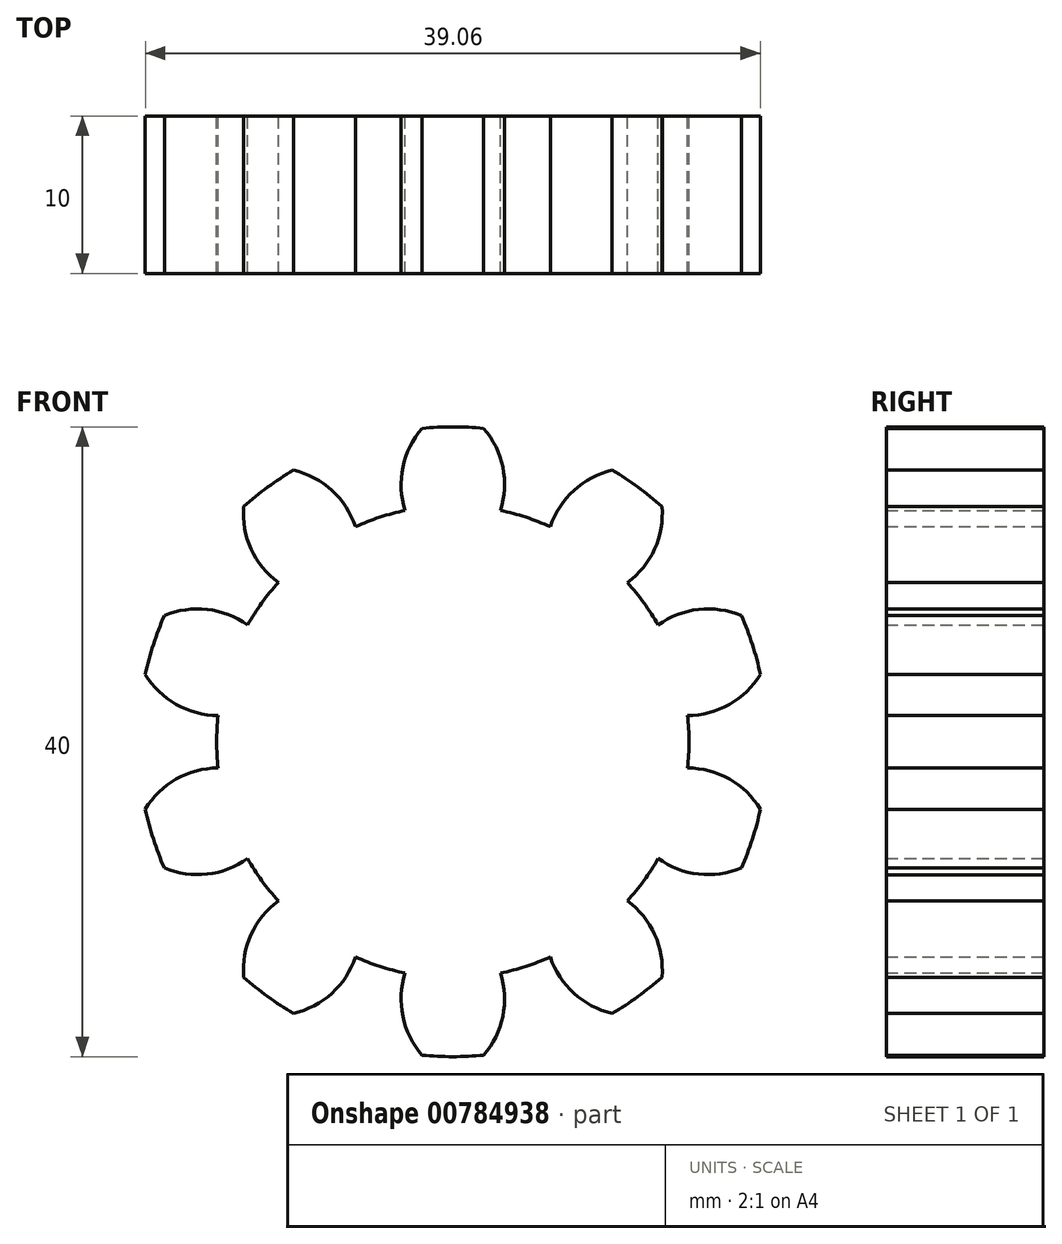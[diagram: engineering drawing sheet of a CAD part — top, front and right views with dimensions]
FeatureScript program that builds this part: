
annotation { "Feature Type Name" : "Feature", "Feature Type Description" : "" }
export const myFeature = defineFeature(function(context is Context, id is Id, definition is map)
    precondition{}
    {
        {
            var Q0;
            Q0=qCreatedBy(makeId("Front.planeOp"),FACE);
            var sketch = newSketch(context, id + "F0", { "sketchPlane" : qUnion([Q0])});
            skArc(sketch, "E0", {"start": v(1.96, 19.9) * mm, "mid": v(0, 20) * mm, "end": v(-1.96, 19.9) * mm});
            skArc(sketch, "E1.0", {"start": v(6.19, 13.66) * mm, "mid": v(4.64, 14.27) * mm, "end": v(3.03, 14.7) * mm});
            skArc(sketch, "E2", {"start": v(3.03, 14.7) * mm, "mid": v(3.17, 17.44) * mm, "end": v(1.96, 19.9) * mm});
            skArc(sketch, "E3.MirrorCS", {"start": v(-3.03, 14.7) * mm, "mid": v(-3.17, 17.44) * mm, "end": v(-1.96, 19.9) * mm});
            skArc(sketch, "E4.1.0", {"start": v(-6.19, 13.66) * mm, "mid": v(-7.68, 15.97) * mm, "end": v(-10.12, 17.25) * mm});
            skArc(sketch, "E4.1.1", {"start": v(-11.08, 10.1) * mm, "mid": v(-12.82, 12.24) * mm, "end": v(-13.28, 14.95) * mm});
            skArc(sketch, "E4.2.0", {"start": v(-13.04, 7.42) * mm, "mid": v(-15.6, 8.4) * mm, "end": v(-18.33, 8.01) * mm});
            skArc(sketch, "E4.2.1", {"start": v(-14.9, 1.66) * mm, "mid": v(-17.56, 2.37) * mm, "end": v(-19.53, 4.3) * mm});
            skArc(sketch, "E5.1.3.0", {"start": v(-14.9, -1.66) * mm, "mid": v(-17.56, -2.37) * mm, "end": v(-19.53, -4.3) * mm});
            skArc(sketch, "E5.4.3.0", {"start": v(-13.04, -7.42) * mm, "mid": v(-15.6, -8.4) * mm, "end": v(-18.33, -8.01) * mm});
            skArc(sketch, "E5.1.4.0", {"start": v(-11.08, -10.1) * mm, "mid": v(-12.82, -12.24) * mm, "end": v(-13.28, -14.95) * mm});
            skArc(sketch, "E5.4.4.0", {"start": v(-6.19, -13.66) * mm, "mid": v(-7.68, -15.97) * mm, "end": v(-10.12, -17.25) * mm});
            skArc(sketch, "E5.1.5.0", {"start": v(-3.03, -14.7) * mm, "mid": v(-3.17, -17.44) * mm, "end": v(-1.96, -19.9) * mm});
            skArc(sketch, "E5.4.5.0", {"start": v(3.03, -14.7) * mm, "mid": v(3.17, -17.44) * mm, "end": v(1.96, -19.9) * mm});
            skArc(sketch, "E5.1.6.0", {"start": v(6.19, -13.66) * mm, "mid": v(7.68, -15.97) * mm, "end": v(10.12, -17.25) * mm});
            skArc(sketch, "E5.4.6.0", {"start": v(11.08, -10.1) * mm, "mid": v(12.82, -12.24) * mm, "end": v(13.28, -14.95) * mm});
            skArc(sketch, "E5.1.7.0", {"start": v(13.04, -7.42) * mm, "mid": v(15.6, -8.4) * mm, "end": v(18.33, -8.01) * mm});
            skArc(sketch, "E5.4.7.0", {"start": v(14.9, -1.66) * mm, "mid": v(17.56, -2.37) * mm, "end": v(19.53, -4.3) * mm});
            skArc(sketch, "E5.1.8.0", {"start": v(14.9, 1.66) * mm, "mid": v(17.56, 2.37) * mm, "end": v(19.53, 4.3) * mm});
            skArc(sketch, "E5.4.8.0", {"start": v(13.04, 7.42) * mm, "mid": v(15.6, 8.4) * mm, "end": v(18.33, 8.01) * mm});
            skArc(sketch, "E5.1.9.0", {"start": v(11.08, 10.1) * mm, "mid": v(12.82, 12.24) * mm, "end": v(13.28, 14.95) * mm});
            skArc(sketch, "E5.4.9.0", {"start": v(6.19, 13.66) * mm, "mid": v(7.68, 15.97) * mm, "end": v(10.12, 17.25) * mm});
            skArc(sketch, "E6.trimOffspring", {"start": v(-10.12, 17.25) * mm, "mid": v(-11.76, 16.18) * mm, "end": v(-13.28, 14.95) * mm});
            skArc(sketch, "E7.trimOffspring", {"start": v(-18.33, 8.01) * mm, "mid": v(-19.02, 6.18) * mm, "end": v(-19.53, 4.3) * mm});
            skArc(sketch, "E8.trimOffspring", {"start": v(-19.53, -4.3) * mm, "mid": v(-19.02, -6.18) * mm, "end": v(-18.33, -8.01) * mm});
            skArc(sketch, "E9.trimOffspring", {"start": v(-13.28, -14.95) * mm, "mid": v(-11.76, -16.18) * mm, "end": v(-10.12, -17.25) * mm});
            skArc(sketch, "E10.trimOffspring", {"start": v(-1.96, -19.9) * mm, "mid": v(0, -20) * mm, "end": v(1.96, -19.9) * mm});
            skArc(sketch, "E11.trimOffspring", {"start": v(10.12, -17.25) * mm, "mid": v(11.76, -16.18) * mm, "end": v(13.28, -14.95) * mm});
            skArc(sketch, "E12.trimOffspring", {"start": v(18.33, -8.01) * mm, "mid": v(19.02, -6.18) * mm, "end": v(19.53, -4.3) * mm});
            skArc(sketch, "E13.trimOffspring", {"start": v(19.53, 4.3) * mm, "mid": v(19.02, 6.18) * mm, "end": v(18.33, 8.01) * mm});
            skArc(sketch, "E14.trimOffspring", {"start": v(13.28, 14.95) * mm, "mid": v(11.76, 16.18) * mm, "end": v(10.12, 17.25) * mm});
            skArc(sketch, "E15.trimOffspring", {"start": v(-3.03, 14.7) * mm, "mid": v(-4.64, 14.27) * mm, "end": v(-6.19, 13.66) * mm});
            skArc(sketch, "E16.trimOffspring", {"start": v(-11.08, 10.1) * mm, "mid": v(-12.14, 8.82) * mm, "end": v(-13.04, 7.42) * mm});
            skArc(sketch, "E17.trimOffspring", {"start": v(-14.9, 1.66) * mm, "mid": v(-15, 0) * mm, "end": v(-14.9, -1.66) * mm});
            skArc(sketch, "E18.trimOffspring", {"start": v(-13.04, -7.42) * mm, "mid": v(-12.14, -8.82) * mm, "end": v(-11.08, -10.1) * mm});
            skArc(sketch, "E19.trimOffspring", {"start": v(-6.19, -13.66) * mm, "mid": v(-4.64, -14.27) * mm, "end": v(-3.03, -14.7) * mm});
            skArc(sketch, "E20.trimOffspring", {"start": v(3.03, -14.7) * mm, "mid": v(4.64, -14.27) * mm, "end": v(6.19, -13.66) * mm});
            skArc(sketch, "E21.trimOffspring", {"start": v(11.08, -10.1) * mm, "mid": v(12.14, -8.82) * mm, "end": v(13.04, -7.42) * mm});
            skArc(sketch, "E22.trimOffspring", {"start": v(14.9, -1.66) * mm, "mid": v(15, 0) * mm, "end": v(14.9, 1.66) * mm});
            skArc(sketch, "E23.trimOffspring", {"start": v(13.04, 7.42) * mm, "mid": v(12.14, 8.82) * mm, "end": v(11.08, 10.1) * mm});
            skSolve(sketch);
        }
        {
            var Q0;
            Q0=makeQuery(id+"F0.imprint","IMPRINT",FACE,{"disambiguationData":[TD([[makeQuery(id+"F0.imprint","IMPRINT",EDGE,{"derivedFrom":sQuery(id+"F0.wireOp",EDGE,"E0")}),1.0]])]});
            extrude(context, id + "F1", {"entities" : qUnion([Q0]), "endBound" : BoundingType.SYMMETRIC, "depth" : 10 * mm, "offsetDistance" : 25 * mm});
        }
    });
